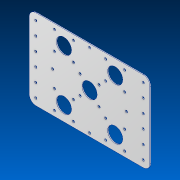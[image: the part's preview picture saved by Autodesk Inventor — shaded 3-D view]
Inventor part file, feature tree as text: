
AUTODESK INVENTOR PART (.ipt)
format: ipt  version: 2022.2 (Build 262287000, 287)  size: 152,576 bytes
history: native  units: in
note: dims shown in document units (in); Inventor stores cm internally (conversion verified against a paired STEP export)
features: other x1, extrude x1, hole x1, sketch x1
ambient origin geometry x8: Origin, YZ Plane, XZ Plane, XY Plane, X Axis, Y Axis, Z Axis, Center Point
bodies: Body1 (feature_tree)
feature tree (4):
  other  "Motor Bracket Outer Panel.ipt"
  extrude  "Extrusion1"  Depth=0.064in TaperAngle=0.0deg
  hole  "Hole1"  [1 undecoded]
  sketch  "Sketch1"  dims[d0=0.3937in d1=0.064in d2=0.0in d3=0.17in d4=0.75in d5=0.375in d6=0.25in d7=0.5635in d8=1.0in d9=0.8108in]
note: 1 required parameter value undecoded (feature->parameter linkage not recoverable at this tier; creation-order binding heuristic only, values carry confidence <= 0.55)
